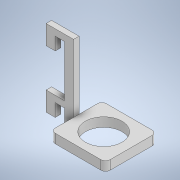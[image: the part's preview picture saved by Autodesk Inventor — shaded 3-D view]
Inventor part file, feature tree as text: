
AUTODESK INVENTOR PART (.ipt)
format: ipt  version: 2020.2 (Build 242310000, 310)  size: 154,624 bytes
history: native  units: in
note: dims shown in document units (in); Inventor stores cm internally (conversion verified against a paired STEP export)
features: extrude x3, sketch x3, fillet x1
ambient origin geometry x8: Origin, YZ Plane, XZ Plane, XY Plane, X Axis, Y Axis, Z Axis, Center Point
bodies: Solid1 (feature_tree)
feature tree (7):
  extrude  "Extrusion1"  Depth=0.175in
  extrude  "Extrusion2"  Depth=0.25in
  extrude  "Extrusion3"  Depth=0.25in
  fillet  "Fillet1"  Radius=0.15in
  sketch  "Sketch1"  dims[d1=1.4in d2=0.175in]
  sketch  "Sketch2"  dims[d3=0.175in d4=0.25in]
  sketch  "Sketch3"  dims[d6=0.25in d7=0.25in d11=0.15in d12=0.0in d13=0.525in d14=0.525in d15=1.5in d16=0.25in d17=1.4in d18=0.0in d19=1.0in d20=1.85in d21=0.0in d22=0.125in]
